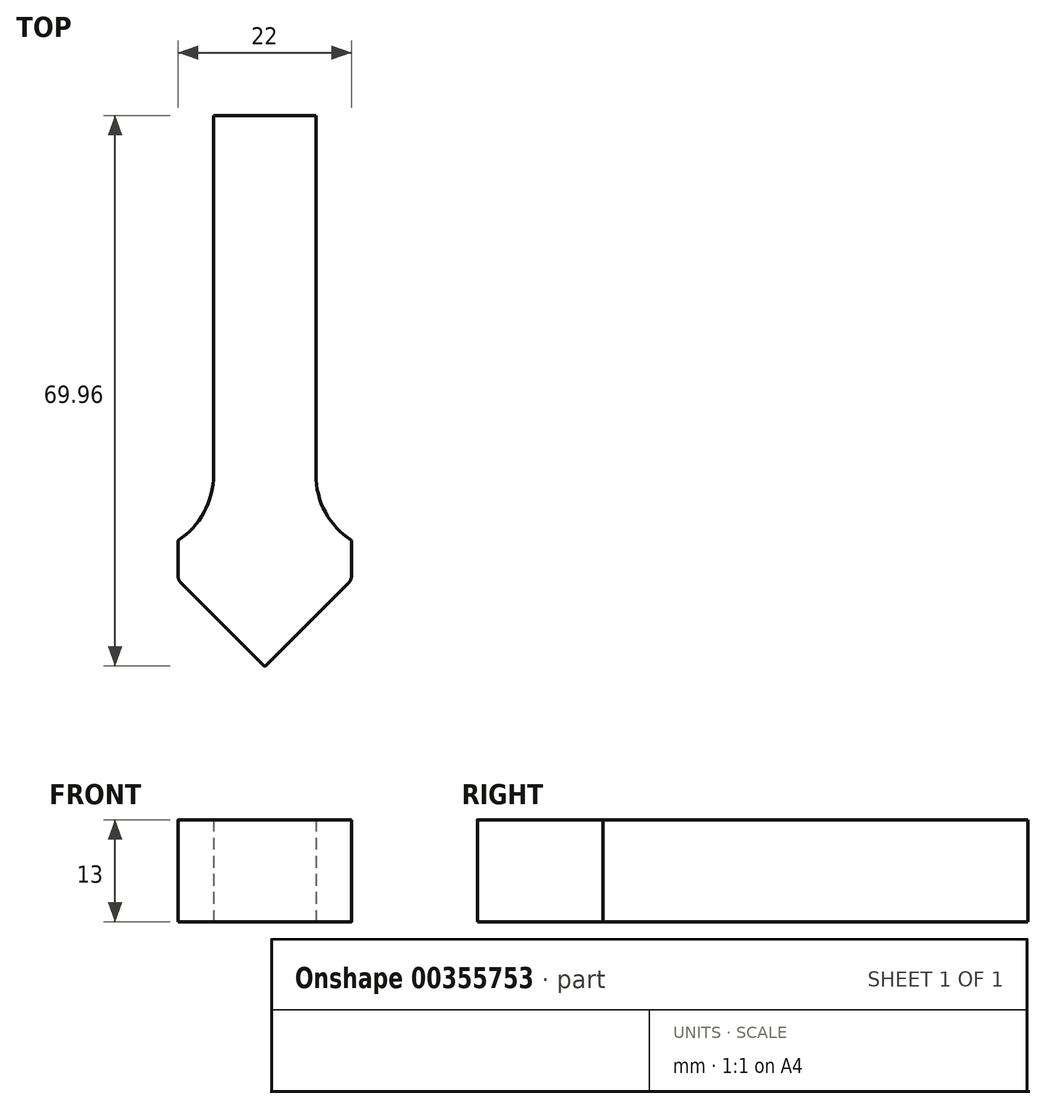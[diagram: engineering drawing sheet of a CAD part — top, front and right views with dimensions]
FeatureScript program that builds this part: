
annotation { "Feature Type Name" : "Feature", "Feature Type Description" : "" }
export const myFeature = defineFeature(function(context is Context, id is Id, definition is map)
    precondition{}
    {
        {
            var Q0;
            Q0=qCreatedBy(makeId("Top.planeOp"),FACE);
            var sketch = newSketch(context, id + "F0", { "sketchPlane" : qUnion([Q0])});
            skLineSegment(sketch, "E0", {"start": v(6.5, 70) * mm, "end": v(0, 70) * mm});
            skLineSegment(sketch, "E1", {"start": v(11, 11) * mm, "end": v(0, 0) * mm});
            skLineSegment(sketch, "E2", {"start": v(6.5, 24.35) * mm, "end": v(6.5, 70) * mm});
            skArc(sketch, "E3", {"start": v(6.5, 24.35) * mm, "mid": v(7.7, 19.6) * mm, "end": v(11, 16) * mm});
            skLineSegment(sketch, "E4", {"start": v(11, 16) * mm, "end": v(11, 11) * mm});
            skLineSegment(sketch, "E5.MirrorCS", {"start": v(-11, 16) * mm, "end": v(-11, 11) * mm});
            skLineSegment(sketch, "E6.MirrorCS", {"start": v(-6.5, 70) * mm, "end": v(0, 70) * mm});
            skLineSegment(sketch, "E7.MirrorCS", {"start": v(-11, 11) * mm, "end": v(0, 0) * mm});
            skArc(sketch, "E8.MirrorCS", {"start": v(-6.5, 24.35) * mm, "mid": v(-7.7, 19.6) * mm, "end": v(-11, 16) * mm});
            skLineSegment(sketch, "E9.MirrorCS", {"start": v(-6.5, 24.35) * mm, "end": v(-6.5, 70) * mm});
            skSolve(sketch);
        }
        {
            var Q0;
            Q0=makeQuery(id+"F0.imprint","IMPRINT",FACE,{"disambiguationData":[TD([[makeQuery(id+"F0.imprint","IMPRINT",EDGE,{"derivedFrom":sQuery(id+"F0.wireOp",EDGE,"E0")}),1.0]])]});
            extrude(context, id + "F1", {"entities" : qUnion([Q0]), "depth" : 13 * mm});
        }
        {
            var Q0;
            Q0=makeQuery(id+"F1.opExtrude","SWEPT_EDGE",EDGE,{"disambiguationData":[OSD([sQuery(id+"F0.wireOp",EDGE,"E1"),sQuery(id+"F0.wireOp",EDGE,"E7.MirrorCS")])]});
            fillet(context, id + "F2", {"entities" : qUnion([Q0]), "radius" : 0.1 * mm, "tangentPropagation" : true, "allowEdgeOverflow" : false});
        }
        {
            var Q0;
            Q0=makeQuery(id+"F1.opExtrude","SWEPT_EDGE",EDGE,{"disambiguationData":[OSD([sQuery(id+"F0.wireOp",EDGE,"E5.MirrorCS"),sQuery(id+"F0.wireOp",EDGE,"E7.MirrorCS")])]});
            var Q1;
            Q1=makeQuery(id+"F1.opExtrude","SWEPT_EDGE",EDGE,{"disambiguationData":[OSD([sQuery(id+"F0.wireOp",EDGE,"E1"),sQuery(id+"F0.wireOp",EDGE,"E4")])]});
            fillet(context, id + "F3", {"entities" : qUnion([Q0, Q1]), "radius" : 1 * mm, "tangentPropagation" : true, "allowEdgeOverflow" : false});
        }
    });
